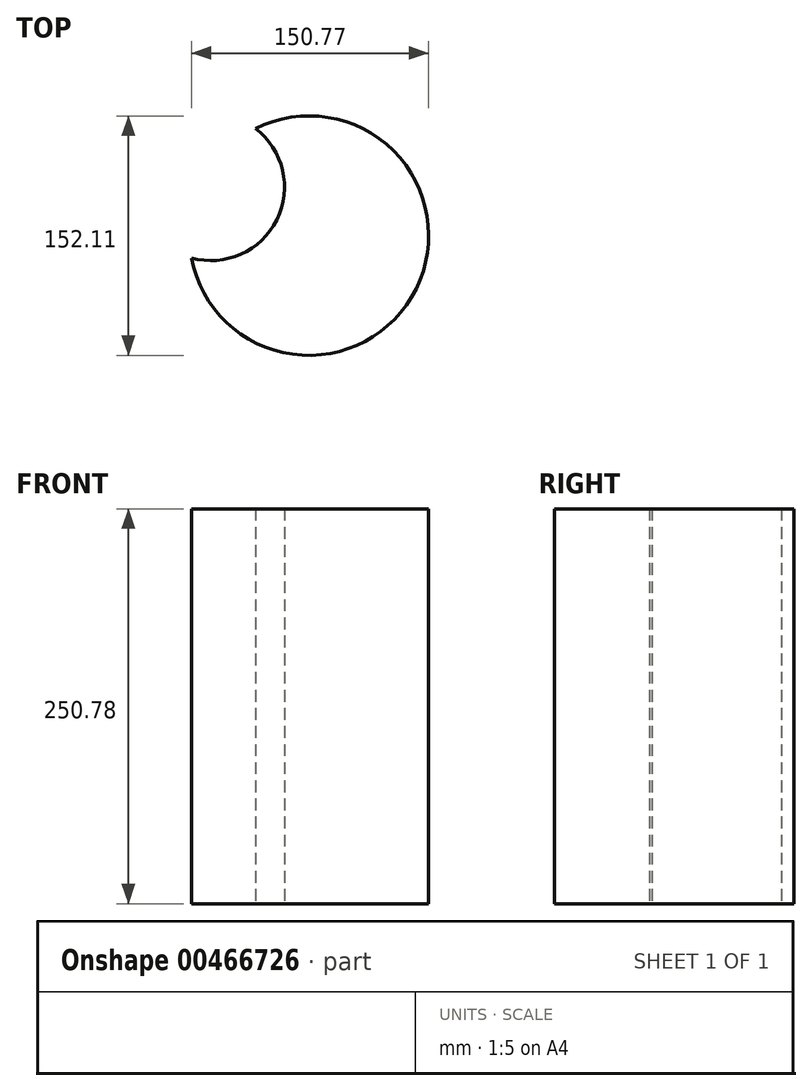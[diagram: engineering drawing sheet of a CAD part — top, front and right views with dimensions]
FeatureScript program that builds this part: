
annotation { "Feature Type Name" : "Feature", "Feature Type Description" : "" }
export const myFeature = defineFeature(function(context is Context, id is Id, definition is map)
    precondition{}
    {
        {
            var Q0;
            Q0=qCreatedBy(makeId("Top.planeOp"),FACE);
            var sketch = newSketch(context, id + "F0", { "sketchPlane" : qUnion([Q0])});
            skCircle(sketch, "E0", {"center": v(73.96, 102.59) * mm, "radius": 41.4 * mm});
            skCircle(sketch, "E1", {"center": v(74.8, 143.98) * mm, "radius": 9.02 * mm});
            skCircle(sketch, "E2", {"center": v(76.92, 152.75) * mm, "radius": 9.02 * mm});
            skSolve(sketch);
        }
        {
            var Q0;
            Q0 = qSketchRegion(id + "F0", true);
            var sketch = newSketch(context, id + "F1", { "sketchPlane" : qUnion([Q0])});
            skCircle(sketch, "E3", {"center": v(166.15, -89.26) * mm, "radius": 11.5 * mm});
            skSolve(sketch);
        }
        {
            var Q0;
            Q0=sQuery(id+"F1.wireOp",EDGE,"E3");
            extrude(context, id + "F2", {"bodyType" : ToolBodyType.SURFACE, "surfaceEntities" : qUnion([Q0]), "depth" : 25.4 * mm});
        }
        {
            var Q0;
            Q0=qCreatedBy(makeId("Top.planeOp"),FACE);
            var sketch = newSketch(context, id + "F3", { "sketchPlane" : qUnion([Q0])});
            skCircle(sketch, "E4", {"center": v(81.46, 0) * mm, "radius": 46.65 * mm});
            skCircle(sketch, "E5", {"center": v(143.67, -30.78) * mm, "radius": 76.05 * mm});
            skSolve(sketch);
        }
        {
            var Q0;
            {var subQ0=sQuery(id+"F3.wireOp",EDGE,"E5");var subQ1=sQuery(id+"F3.wireOp",EDGE,"E4");var subQ2=makeQuery(id+"F3.imprint","INTERSECT",VERTEX,{"disambiguationData":[OD(0.0)],"derivedFrom":[subQ1,subQ0]});Q0=makeQuery(id+"F3.imprint","IMPRINT",FACE,{"disambiguationData":[TD([[makeQuery(id+"F3.imprint","IMPRINT",EDGE,{"disambiguationData":[TD([[subQ2,-1.0]])],"derivedFrom":subQ1}),-1.0]])]});}
            extrude(context, id + "F4", {"entities" : qUnion([Q0]), "depth" : 250.78 * mm});
        }
    });
